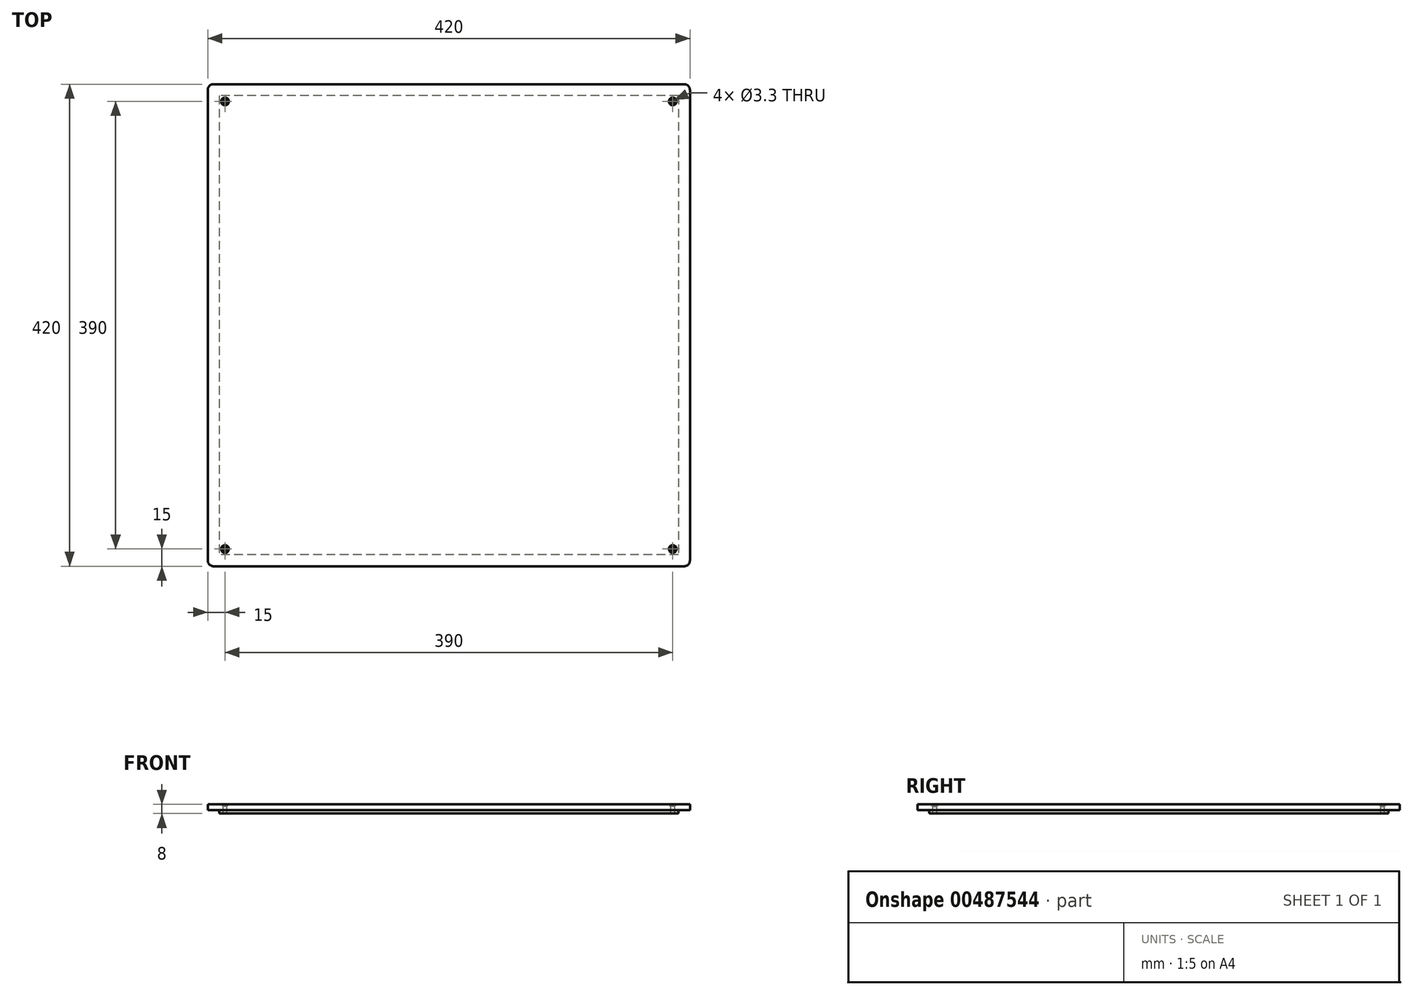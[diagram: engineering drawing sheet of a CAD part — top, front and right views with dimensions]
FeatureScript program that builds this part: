
annotation { "Feature Type Name" : "Feature", "Feature Type Description" : "" }
export const myFeature = defineFeature(function(context is Context, id is Id, definition is map)
    precondition{}
    {
        {
            var Q0;
            Q0=qCreatedBy(makeId("Top.planeOp"),FACE);
            var sketch = newSketch(context, id + "F0", { "sketchPlane" : qUnion([Q0])});
            skLineSegment(sketch, "E0.bottom", {"start": v(210, -210) * mm, "end": v(-210, -210) * mm});
            skLineSegment(sketch, "E0.top", {"start": v(210, 210) * mm, "end": v(-210, 210) * mm});
            skLineSegment(sketch, "E0.left", {"start": v(210, -210) * mm, "end": v(210, 210) * mm});
            skLineSegment(sketch, "E0.right", {"start": v(-210, -210) * mm, "end": v(-210, 210) * mm});
            skPoint(sketch, "E0.middle", {"position": v(0, 0) * mm});
            skPoint(sketch, "E1", {"position": v(-195, 195) * mm});
            skPoint(sketch, "E2.MirrorP", {"position": v(195, 195) * mm});
            skPoint(sketch, "E3.MirrorP", {"position": v(195, -195) * mm});
            skPoint(sketch, "E4.MirrorP", {"position": v(-195, -195) * mm});
            skSolve(sketch);
        }
        {
            var Q0;
            Q0=makeQuery(id+"F0.imprint","IMPRINT",FACE,{"disambiguationData":[TD([[makeQuery(id+"F0.imprint","IMPRINT",EDGE,{"derivedFrom":sQuery(id+"F0.wireOp",EDGE,"E0.bottom")}),-1.0]])]});
            extrude(context, id + "F1", {"entities" : qUnion([Q0]), "oppositeDirection" : true, "depth" : 5 * mm, "offsetDistance" : 25 * mm});
        }
        {
            var Q0;
            Q0=makeQuery(id+"F1.opExtrude","SWEPT_EDGE",EDGE,{"disambiguationData":[OSD([sQuery(id+"F0.wireOp",EDGE,"E0.bottom"),sQuery(id+"F0.wireOp",EDGE,"E0.right")])]});
            var Q1;
            Q1=makeQuery(id+"F1.opExtrude","SWEPT_EDGE",EDGE,{"disambiguationData":[OSD([sQuery(id+"F0.wireOp",EDGE,"E0.top"),sQuery(id+"F0.wireOp",EDGE,"E0.right")])]});
            var Q2;
            Q2=makeQuery(id+"F1.opExtrude","SWEPT_EDGE",EDGE,{"disambiguationData":[OSD([sQuery(id+"F0.wireOp",EDGE,"E0.top"),sQuery(id+"F0.wireOp",EDGE,"E0.left")])]});
            var Q3;
            Q3=makeQuery(id+"F1.opExtrude","SWEPT_EDGE",EDGE,{"disambiguationData":[OSD([sQuery(id+"F0.wireOp",EDGE,"E0.bottom"),sQuery(id+"F0.wireOp",EDGE,"E0.left")])]});
            fillet(context, id + "F2", {"entities" : qUnion([Q0, Q1, Q2, Q3]), "radius" : 5 * mm, "tangentPropagation" : true, "allowEdgeOverflow" : false});
        }
        {
            var Q0;
            Q0=sQuery(id+"F0.wireOp",VERTEX,"E1");
            var Q1;
            Q1=sQuery(id+"F0.wireOp",VERTEX,"E2.MirrorP");
            var Q2;
            Q2=sQuery(id+"F0.wireOp",VERTEX,"E3.MirrorP");
            var Q3;
            Q3=sQuery(id+"F0.wireOp",VERTEX,"E4.MirrorP");
            var Q4;
            Q4=makeQuery(id+"F1.opExtrude","SWEPT_BODY",BODY,{"disambiguationData":[OSD([sQuery(id+"F0.wireOp",EDGE,"E0.bottom"),sQuery(id+"F0.wireOp",EDGE,"E0.top"),sQuery(id+"F0.wireOp",EDGE,"E0.left"),sQuery(id+"F0.wireOp",EDGE,"E0.right")])]});
            hole(context, id + "F3", {"style" : HoleStyle.C_SINK, "endStyle" : HoleEndStyle.THROUGH, "standardTappedOrClearance" : lookupTablePath({ "standard" : "ISO", "fit" : "Normal", "size" : "M3", "type" : "Clearance" }), "standardBlindInLast" : lookupTablePath({ "fit" : "Standard", "standard" : "ISO", "size" : "M3", "type" : "Clearance" }), "holeDiameter" : 3.3 * mm, "cSinkDiameter" : 6.72 * mm, "cSinkAngle" : 90 * degree, "isTappedThrough" : true, "tappedDepth" : 12 * mm, "tapClearance" : 3, "locations" : qUnion([Q0, Q1, Q2, Q3]), "scope" : qUnion([Q4])});
        }
        {
            var Q0;
            Q0=makeQuery(id+"F1.opExtrude","CAP_FACE",FACE,{"disambiguationData":[OSD([sQuery(id+"F0.wireOp",EDGE,"E0.bottom"),sQuery(id+"F0.wireOp",EDGE,"E0.top"),sQuery(id+"F0.wireOp",EDGE,"E0.left"),sQuery(id+"F0.wireOp",EDGE,"E0.right")])],"isStart":false});
            var sketch = newSketch(context, id + "F4", { "sketchPlane" : qUnion([Q0])});
            skLineSegment(sketch, "E5.bottom", {"start": v(200, -200) * mm, "end": v(-200, -200) * mm});
            skLineSegment(sketch, "E5.top", {"start": v(200, 200) * mm, "end": v(-200, 200) * mm});
            skLineSegment(sketch, "E5.left", {"start": v(200, -200) * mm, "end": v(200, 200) * mm});
            skLineSegment(sketch, "E5.right", {"start": v(-200, -200) * mm, "end": v(-200, 200) * mm});
            skPoint(sketch, "E5.middle", {"position": v(0, 0) * mm});
            skSolve(sketch);
        }
        {
            var Q0;
            Q0=makeQuery(id+"F4.imprint","IMPRINT",FACE,{"disambiguationData":[TD([[makeQuery(id+"F4.imprint","IMPRINT",EDGE,{"derivedFrom":sQuery(id+"F4.wireOp",EDGE,"E5.bottom")}),-1.0]])]});
            extrude(context, id + "F5", {"entities" : qUnion([Q0]), "operationType" : NewBodyOperationType.ADD, "depth" : 3 * mm, "offsetDistance" : 25 * mm});
        }
    });
